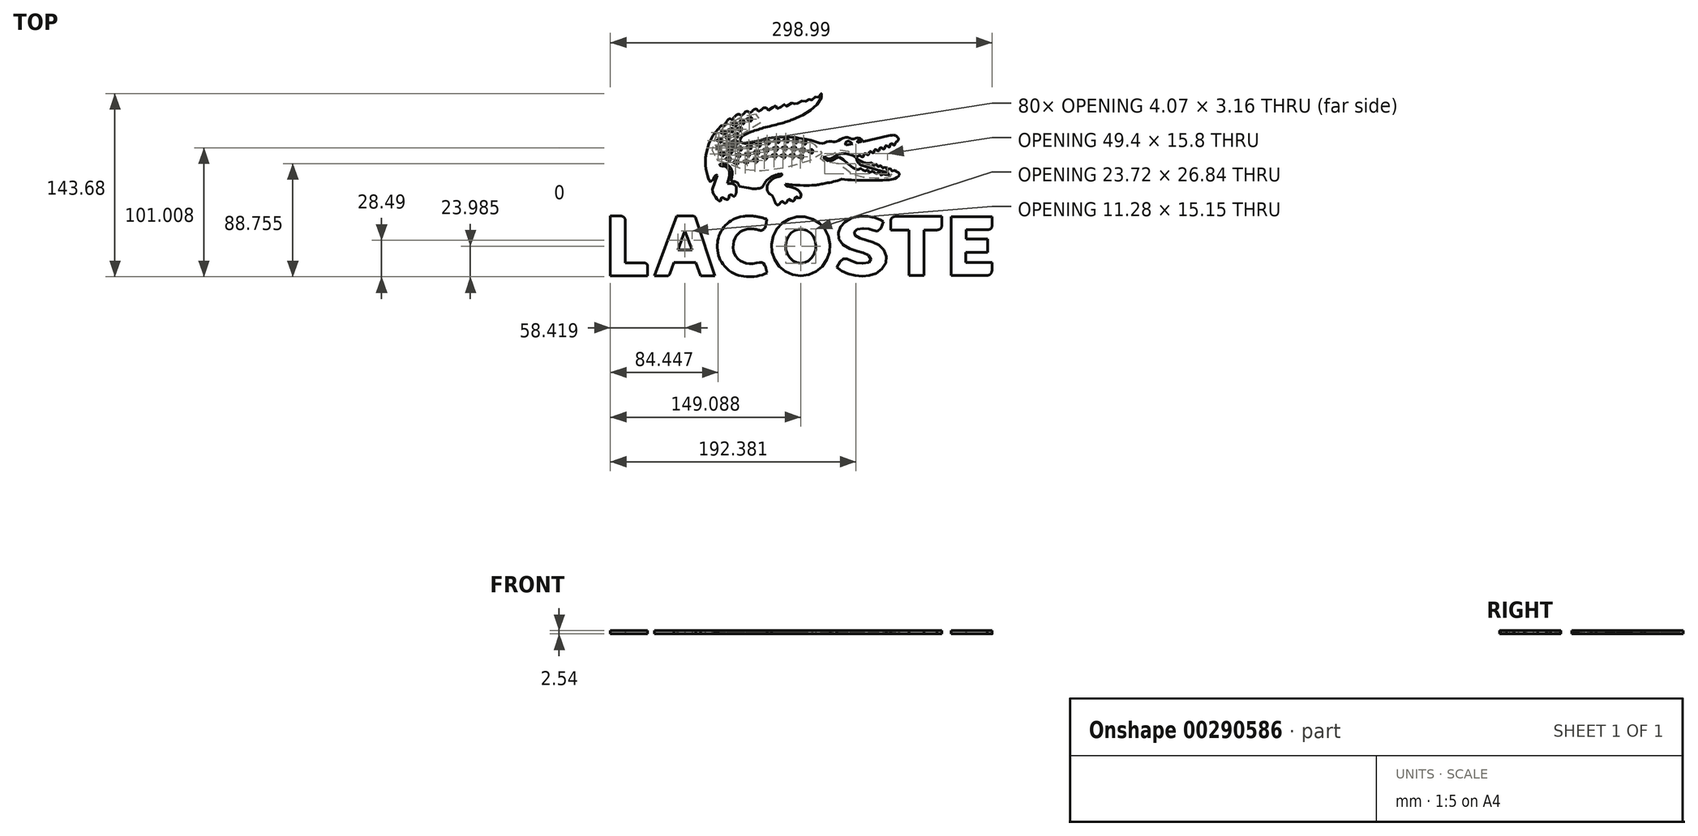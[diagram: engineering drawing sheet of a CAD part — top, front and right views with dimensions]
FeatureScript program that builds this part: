
annotation { "Feature Type Name" : "Feature", "Feature Type Description" : "" }
export const myFeature = defineFeature(function(context is Context, id is Id, definition is map)
    precondition{}
    {
        {
            var Q0;
            Q0=qCreatedBy(makeId("Top.planeOp"),FACE);
            var sketch = newSketch(context, id + "F0", { "sketchPlane" : qUnion([Q0])});
            skLineSegment(sketch, "E0", {"start": v(-126.74, -26.36) * mm, "end": v(-126.74, -73.35) * mm});
            skLineSegment(sketch, "E1", {"start": v(-126.74, -73.35) * mm, "end": v(-97.53, -73.35) * mm});
            skLineSegment(sketch, "E2", {"start": v(-97.53, -73.35) * mm, "end": v(-97.53, -65.73) * mm});
            skLineSegment(sketch, "E3", {"start": v(-100.07, -63.19) * mm, "end": v(-115.19, -63.19) * mm});
            skPoint(sketch, "E4.visualSharp", {"position": v(-97.53, -63.19) * mm});
            skArc(sketch, "E4.filletArc", {"start": v(-97.53, -65.73) * mm, "mid": v(-98.27, -63.93) * mm, "end": v(-100.07, -63.19) * mm});
            skPoint(sketch, "E5.visualSharp", {"position": v(-115.38, -25.09) * mm});
            skLineSegment(sketch, "E6", {"start": v(-126.74, -26.36) * mm, "end": v(-118.4, -26.36) * mm});
            skLineSegment(sketch, "E7", {"start": v(-115.22, -29.53) * mm, "end": v(-115.19, -63.19) * mm});
            skPoint(sketch, "E8.visualSharp", {"position": v(-115.22, -26.36) * mm});
            skArc(sketch, "E8.filletArc", {"start": v(-115.22, -29.53) * mm, "mid": v(-116.15, -27.29) * mm, "end": v(-118.4, -26.36) * mm});
            skLineSegment(sketch, "E9", {"start": v(-92.44, -73.35) * mm, "end": v(-74.98, -26.36) * mm});
            skLineSegment(sketch, "E10", {"start": v(-74.98, -26.36) * mm, "end": v(-62.15, -26.35) * mm});
            skLineSegment(sketch, "E11", {"start": v(-59.73, -28.1) * mm, "end": v(-45.04, -73.35) * mm});
            skLineSegment(sketch, "E12", {"start": v(-45.04, -73.35) * mm, "end": v(-56.2, -73.36) * mm});
            skLineSegment(sketch, "E13", {"start": v(-56.2, -73.36) * mm, "end": v(-59.86, -62.9) * mm});
            skLineSegment(sketch, "E14", {"start": v(-59.86, -62.9) * mm, "end": v(-77.03, -62.9) * mm});
            skLineSegment(sketch, "E15", {"start": v(-77.03, -62.9) * mm, "end": v(-80.3, -71.7) * mm});
            skLineSegment(sketch, "E16", {"start": v(-82.68, -73.35) * mm, "end": v(-92.44, -73.35) * mm});
            skPoint(sketch, "E17.visualSharp", {"position": v(-80.92, -73.35) * mm});
            skArc(sketch, "E17.filletArc", {"start": v(-82.68, -73.35) * mm, "mid": v(-81.23, -72.9) * mm, "end": v(-80.3, -71.7) * mm});
            skPoint(sketch, "E18.visualSharp", {"position": v(-60.3, -26.35) * mm});
            skArc(sketch, "E18.filletArc", {"start": v(-59.73, -28.1) * mm, "mid": v(-60.66, -26.83) * mm, "end": v(-62.15, -26.35) * mm});
            skLineSegment(sketch, "E19", {"start": v(-73.96, -53.02) * mm, "end": v(-68.33, -37.86) * mm});
            skLineSegment(sketch, "E20", {"start": v(-73.96, -53.02) * mm, "end": v(-62.68, -53.02) * mm});
            skLineSegment(sketch, "E21", {"start": v(-62.68, -53.02) * mm, "end": v(-68.33, -37.86) * mm});
            skArc(sketch, "E22", {"start": v(-22.8, -26.67) * mm, "mid": v(-36.65, -33.59) * mm, "end": v(-42.88, -47.77) * mm});
            skFitSpline(sketch, "E23", {"points": [v(-22.8, -26.67) * mm, v(-12.94, -26.67) * mm, v(-4.25, -28.89) * mm], "startDerivative": vector(21.68, 4.28) * mm, "endDerivative": vector(17.37, -6.77) * mm});
            skFitSpline(sketch, "E24", {"points": [v(-4.25, -28.89) * mm, v(-5.17, -33.86) * mm, v(-6.83, -36.92) * mm, v(-9.2, -37.59) * mm, v(-12.8, -36.7) * mm, v(-19.15, -36.46) * mm], "startDerivative": vector(-3.17, -23.27) * mm, "endDerivative": vector(-27.28, -0.67) * mm});
            skFitSpline(sketch, "E25", {"points": [v(-19.15, -36.46) * mm, v(-22.65, -37.5) * mm, v(-26.5, -39.93) * mm, v(-29.25, -43.78) * mm, v(-30.5, -49.4) * mm, v(-29.9, -55.03) * mm, v(-27.1, -59.6) * mm, v(-22.68, -62.67) * mm, v(-16.57, -63.79) * mm, v(-9.58, -62.6) * mm, v(-7.29, -62.94) * mm, v(-5.65, -65.1) * mm, v(-4.15, -70.91) * mm], "startDerivative": vector(-47.82, -11.43) * mm, "endDerivative": vector(13.68, -69.44) * mm});
            skArc(sketch, "E26", {"start": v(-42.88, -47.77) * mm, "mid": v(-42.97, -51.46) * mm, "end": v(-42.43, -55.11) * mm});
            skPoint(sketch, "E27.center.orphan", {"position": v(-20.17, -53.24) * mm});
            skFitSpline(sketch, "E28", {"points": [v(-42.43, -55.11) * mm, v(-39.32, -63.08) * mm, v(-31.41, -70.65) * mm, v(-22.68, -73.62) * mm, v(-13.21, -73.62) * mm, v(-4.15, -70.91) * mm], "startDerivative": vector(7.53, -52.18) * mm, "endDerivative": vector(40.9, 22.15) * mm});
            skArc(sketch, "E29.trimOffspring", {"start": v(-5.77, -64.84) * mm, "mid": v(-4.42, -63.24) * mm, "end": v(-3.23, -61.53) * mm});
            skEllipse(sketch, "E30", {"center": v(22.35, -49.95) * mm, "majorRadius": 23.23 * mm, "minorRadius": 23.02 * mm, "majorAxis": v(0, -1)});
            skEllipse(sketch, "E31", {"center": v(22.35, -49.95) * mm, "majorRadius": 13.42 * mm, "minorRadius": 11.86 * mm, "majorAxis": v(0, -1)});
            skFitSpline(sketch, "E32", {"points": [v(87.17, -30.8) * mm, v(83.6, -28.79) * mm, v(76.69, -27) * mm, v(64.74, -27.08) * mm, v(54.98, -32.69) * mm, v(51.81, -39.35) * mm, v(53.6, -46.83) * mm, v(63.52, -52.93) * mm, v(71.54, -55.3) * mm, v(76.45, -58.13) * mm, v(77.01, -61.55) * mm, v(72.14, -63.5) * mm, v(64.82, -62.6) * mm, v(59.94, -60.5) * mm, v(56.85, -59.52) * mm, v(54.25, -60.74) * mm, v(50.67, -66.59) * mm], "startDerivative": vector(-65.13, 47.63) * mm, "endDerivative": vector(-55.42, -106.59) * mm});
            skFitSpline(sketch, "E33", {"points": [v(50.67, -66.59) * mm, v(58.36, -71.4) * mm, v(69.3, -73.41) * mm, v(80.26, -71.73) * mm, v(88.4, -64.32) * mm, v(88.4, -54.72) * mm, v(81.08, -47.8) * mm, v(71.73, -44.72) * mm, v(64.9, -41.55) * mm, v(64.25, -39.11) * mm, v(67.26, -36.5) * mm, v(75.01, -36.34) * mm, v(78.67, -37.37) * mm, v(83.24, -38) * mm, v(87.17, -30.8) * mm], "startDerivative": vector(73.41, -63) * mm, "endDerivative": vector(50.37, 126.81) * mm});
            skLineSegment(sketch, "E34", {"start": v(107.14, -73.07) * mm, "end": v(107.14, -37.39) * mm});
            skLineSegment(sketch, "E35", {"start": v(107.14, -37.39) * mm, "end": v(92.8, -37.39) * mm});
            skLineSegment(sketch, "E36", {"start": v(92.8, -37.39) * mm, "end": v(92.8, -30.06) * mm});
            skLineSegment(sketch, "E37", {"start": v(107.14, -73.07) * mm, "end": v(118.77, -73.07) * mm});
            skLineSegment(sketch, "E38", {"start": v(118.77, -73.07) * mm, "end": v(118.77, -37.28) * mm});
            skLineSegment(sketch, "E39", {"start": v(118.77, -37.28) * mm, "end": v(129.11, -37.28) * mm});
            skFitSpline(sketch, "E40", {"points": [v(92.8, -30.06) * mm, v(93.55, -27.9) * mm, v(96.03, -26.72) * mm], "startDerivative": vector(0.83, 5.06) * mm, "endDerivative": vector(5.56, 1.68) * mm});
            skLineSegment(sketch, "E41", {"start": v(96.03, -26.72) * mm, "end": v(132.77, -26.72) * mm});
            skLineSegment(sketch, "E42", {"start": v(132.77, -26.72) * mm, "end": v(132.77, -34.2) * mm});
            skFitSpline(sketch, "E43", {"points": [v(129.11, -37.28) * mm, v(131.7, -36.34) * mm, v(132.77, -34.2) * mm], "startDerivative": vector(6.35, 1.16) * mm, "endDerivative": vector(1.9, 7.6) * mm});
            skLineSegment(sketch, "E44", {"start": v(172.25, -33.98) * mm, "end": v(172.25, -26.74) * mm});
            skLineSegment(sketch, "E45", {"start": v(172.25, -26.74) * mm, "end": v(140.16, -26.74) * mm});
            skLineSegment(sketch, "E46", {"start": v(140.16, -26.74) * mm, "end": v(140.16, -73) * mm});
            skLineSegment(sketch, "E47", {"start": v(140.16, -73) * mm, "end": v(168.36, -73) * mm});
            skLineSegment(sketch, "E48", {"start": v(172.17, -68.8) * mm, "end": v(172.17, -62.63) * mm});
            skLineSegment(sketch, "E49", {"start": v(172.17, -62.63) * mm, "end": v(151.6, -62.63) * mm});
            skLineSegment(sketch, "E50", {"start": v(151.6, -62.63) * mm, "end": v(151.6, -54.79) * mm});
            skLineSegment(sketch, "E51", {"start": v(151.6, -54.79) * mm, "end": v(168.59, -54.79) * mm});
            skLineSegment(sketch, "E52", {"start": v(168.59, -54.79) * mm, "end": v(168.59, -44.27) * mm});
            skLineSegment(sketch, "E53", {"start": v(168.59, -44.27) * mm, "end": v(151.75, -44.27) * mm});
            skLineSegment(sketch, "E54", {"start": v(151.75, -44.27) * mm, "end": v(151.75, -37.18) * mm});
            skLineSegment(sketch, "E55", {"start": v(151.75, -37.18) * mm, "end": v(168.36, -37.18) * mm});
            skFitSpline(sketch, "E56", {"points": [v(168.36, -37.18) * mm, v(171.1, -36.34) * mm, v(172.25, -33.98) * mm], "startDerivative": vector(6.59, 0.9) * mm, "endDerivative": vector(1.87, 7.95) * mm});
            skFitSpline(sketch, "E57", {"points": [v(172.17, -68.8) * mm, v(170.95, -71.78) * mm, v(168.36, -73) * mm], "startDerivative": vector(-1.37, -10.07) * mm, "endDerivative": vector(-10.1, -1.84) * mm});
            skSolve(sketch);
        }
        {
            var Q0;
            Q0=makeQuery(id+"F0.imprint","IMPRINT",FACE,{"disambiguationData":[TD([[makeQuery(id+"F0.imprint","IMPRINT",EDGE,{"derivedFrom":sQuery(id+"F0.wireOp",EDGE,"E0")}),1.0]])]});
            var Q1;
            Q1=makeQuery(id+"F0.imprint","IMPRINT",FACE,{"disambiguationData":[TD([[makeQuery(id+"F0.imprint","IMPRINT",EDGE,{"derivedFrom":sQuery(id+"F0.wireOp",EDGE,"E9")}),-1.0]])]});
            var Q2;
            Q2=makeQuery(id+"F0.imprint","IMPRINT",FACE,{"disambiguationData":[TD([[makeQuery(id+"F0.imprint","IMPRINT",EDGE,{"derivedFrom":sQuery(id+"F0.wireOp",EDGE,"E22")}),1.0]])]});
            var Q3;
            Q3=makeQuery(id+"F0.imprint","IMPRINT",FACE,{"disambiguationData":[TD([[makeQuery(id+"F0.imprint","IMPRINT",EDGE,{"derivedFrom":sQuery(id+"F0.wireOp",EDGE,"E30")}),1.0]])]});
            var Q4;
            Q4=makeQuery(id+"F0.imprint","IMPRINT",FACE,{"disambiguationData":[TD([[makeQuery(id+"F0.imprint","IMPRINT",EDGE,{"derivedFrom":sQuery(id+"F0.wireOp",EDGE,"E32")}),1.0]])]});
            var Q5;
            Q5=makeQuery(id+"F0.imprint","IMPRINT",FACE,{"disambiguationData":[TD([[makeQuery(id+"F0.imprint","IMPRINT",EDGE,{"derivedFrom":sQuery(id+"F0.wireOp",EDGE,"E34")}),-1.0]])]});
            var Q6;
            Q6=makeQuery(id+"F0.imprint","IMPRINT",FACE,{"disambiguationData":[TD([[makeQuery(id+"F0.imprint","IMPRINT",EDGE,{"derivedFrom":sQuery(id+"F0.wireOp",EDGE,"E44")}),1.0]])]});
            extrude(context, id + "F1", {"entities" : qUnion([Q0, Q1, Q2, Q3, Q4, Q5, Q6]), "depth" : 2.54 * mm});
        }
        {
            var Q0;
            Q0=qCreatedBy(makeId("Top.planeOp"),FACE);
            var sketch = newSketch(context, id + "F2", { "sketchPlane" : qUnion([Q0])});
            skFitSpline(sketch, "E58", {"points": [v(-33.16, -9.8) * mm, v(-31.82, -9.75) * mm, v(-30.48, -10.73) * mm, v(-29.55, -10.73) * mm, v(-28.16, -8.13) * mm], "startDerivative": vector(6.07, 1.44) * mm, "endDerivative": vector(3.91, 9.96) * mm});
            skFitSpline(sketch, "E59", {"points": [v(-28.16, -8.13) * mm, v(-28.16, -3.92) * mm], "startDerivative": vector(0, 4.22) * mm, "endDerivative": vector(0, 4.22) * mm});
            skFitSpline(sketch, "E60", {"points": [v(-28.16, -3.92) * mm, v(-28.6, -2.62) * mm, v(-30.38, -1.28) * mm], "startDerivative": vector(-0.87, 3.34) * mm, "endDerivative": vector(-3.8, 2.24) * mm});
            skFitSpline(sketch, "E61", {"points": [v(-30.38, -1.28) * mm, v(-35.23, -0.71) * mm], "startDerivative": vector(-3.93, 1.7) * mm, "endDerivative": vector(-4.72, 0.42) * mm});
            skFitSpline(sketch, "E62", {"points": [v(-35.23, -0.71) * mm, v(-33.63, 5.12) * mm, v(-33.7, 8.88) * mm, v(-35.23, 11.4) * mm, v(-37.41, 12.77) * mm, v(-40.35, 13) * mm, v(-40.9, 13.42) * mm, v(-41.08, 14.3) * mm], "startDerivative": vector(4.9, 23.15) * mm, "endDerivative": vector(2.82, 11.86) * mm});
            skFitSpline(sketch, "E63", {"points": [v(-33.16, -9.8) * mm, v(-33.68, -10.3) * mm, v(-34.2, -12.63) * mm, v(-35.09, -13.47) * mm, v(-36.8, -13.01) * mm, v(-38.13, -12.14) * mm, v(-39.5, -11.95) * mm, v(-40.15, -12.7) * mm, v(-40.27, -13.97) * mm, v(-40.73, -14.58) * mm, v(-41.87, -14.39) * mm, v(-46.63, -7.9) * mm], "startDerivative": vector(-9.57, -5.5) * mm, "endDerivative": vector(-26.48, 42.47) * mm});
            skFitSpline(sketch, "E64", {"points": [v(-46.63, -7.9) * mm, v(-46.84, -5.25) * mm], "startDerivative": vector(-0.21, 2.66) * mm, "endDerivative": vector(-0.21, 2.66) * mm});
            skFitSpline(sketch, "E65", {"points": [v(-46.84, -5.25) * mm, v(-43.16, 5.41) * mm], "startDerivative": vector(3.68, 10.66) * mm, "endDerivative": vector(3.68, 10.66) * mm});
            skFitSpline(sketch, "E66", {"points": [v(-43.16, 5.41) * mm, v(-43.16, 5.76) * mm, v(-44.08, 5.76) * mm, v(-45.18, 4.72) * mm, v(-46.63, 1.75) * mm, v(-47.86, 0.87) * mm, v(-48.8, 0.8) * mm, v(-50.1, 3.4) * mm, v(-51.72, 10.2) * mm, v(-52.08, 20.08) * mm, v(-47.82, 34.36) * mm, v(-40.35, 44.17) * mm], "startDerivative": vector(4.33, 14.89) * mm, "endDerivative": vector(50.94, 58.96) * mm});
            skFitSpline(sketch, "E67", {"points": [v(-40.35, 44.17) * mm, v(-39.97, 44.74) * mm, v(-38.78, 44.17) * mm, v(-34.54, 49.27) * mm, v(-33.1, 49.85) * mm, v(-32.1, 49.25) * mm], "startDerivative": vector(6.96, 5.98) * mm, "endDerivative": vector(5.99, -6.7) * mm});
            skFitSpline(sketch, "E68", {"points": [v(-32.1, 49.25) * mm, v(-31.52, 49.25) * mm, v(-30.26, 50.46) * mm, v(-27.02, 53.55) * mm, v(-25.48, 53.16) * mm, v(-24.3, 52.62) * mm, v(-21.92, 54.34) * mm, v(-20.48, 55.61) * mm, v(-19, 55.9) * mm, v(-18.44, 55.09) * mm, v(-17.22, 54.77) * mm, v(-15.03, 56.62) * mm, v(-13.23, 57.63) * mm], "startDerivative": vector(12.35, -2.62) * mm, "endDerivative": vector(20.2, 8.3) * mm});
            skFitSpline(sketch, "E69", {"points": [v(-13.23, 57.63) * mm, v(-12.27, 57.63) * mm, v(-11.4, 56.4) * mm, v(-10.95, 56.05) * mm, v(-10.18, 56) * mm, v(-6.53, 58.68) * mm], "startDerivative": vector(6.18, 1.68) * mm, "endDerivative": vector(11.93, 10.26) * mm});
            skFitSpline(sketch, "E70", {"points": [v(-6.53, 58.68) * mm, v(-5.67, 59.01) * mm, v(-4.8, 58.68) * mm, v(-4.54, 57.83) * mm, v(-3.8, 57) * mm, v(-2.23, 56.86) * mm, v(0.65, 59.3) * mm, v(1.88, 60.13) * mm, v(2.7, 59.99) * mm, v(3.13, 59.06) * mm, v(3.85, 58.04) * mm, v(4.97, 57.83) * mm, v(7.1, 59.53) * mm, v(9.08, 61.1) * mm, v(9.9, 60.91) * mm, v(10.6, 60) * mm, v(11.38, 59.78) * mm, v(15.66, 62.34) * mm, v(16.39, 62.34) * mm, v(17.22, 61.8) * mm, v(18.35, 61.35) * mm, v(19.3, 61.48) * mm, v(22.07, 64.04) * mm, v(24.36, 63.18) * mm, v(25.6, 63.12) * mm, v(27.81, 65.06) * mm, v(29.13, 65.12) * mm, v(29.7, 64.58) * mm, v(30.75, 64.47) * mm, v(32.8, 66.65) * mm, v(34.03, 66.94) * mm, v(35.12, 66.6) * mm, v(36.24, 66.94) * mm, v(38.17, 69.63) * mm, v(38.72, 69.6) * mm, v(38.6, 66.7) * mm, v(34.57, 60.62) * mm, v(27.65, 55.04) * mm, v(15.85, 49.25) * mm], "startDerivative": vector(44.69, 26.17) * mm, "endDerivative": vector(-212.73, -79.77) * mm});
            skFitSpline(sketch, "E71", {"points": [v(-41.08, 14.3) * mm, v(-37.29, 14.3) * mm, v(-33.9, 13) * mm, v(-31.7, 9.7) * mm, v(-31.37, 6.35) * mm, v(-32.21, 0.9) * mm], "startDerivative": vector(19.64, 1.15) * mm, "endDerivative": vector(-3.96, -20.19) * mm});
            skFitSpline(sketch, "E72", {"points": [v(-32.21, 0.9) * mm, v(-29.12, 0.61) * mm, v(-27.6, 0) * mm, v(-26.56, -1.29) * mm, v(-25.95, -2.96) * mm], "startDerivative": vector(9.82, -0.81) * mm, "endDerivative": vector(2.23, -7.43) * mm});
            skFitSpline(sketch, "E73", {"points": [v(-25.95, -2.96) * mm, v(-17, -4.67) * mm, v(-12.13, -4.85) * mm, v(-8.22, -3.84) * mm, v(-6.01, -0.8) * mm, v(-2.33, 3.23) * mm, v(4.19, 6.29) * mm, v(7.33, 6.67) * mm, v(7.6, 6.08) * mm, v(6.06, 4.9) * mm, v(3.84, 4.35) * mm, v(0, 2.54) * mm, v(-4.04, -3.23) * mm, v(-2.75, -8.37) * mm, v(0, -10.45) * mm, v(2.8, -16.61) * mm, v(4.26, -17.66) * mm], "startDerivative": vector(101.91, -23.85) * mm, "endDerivative": vector(37.13, -13.37) * mm});
            skFitSpline(sketch, "E74", {"points": [v(4.19, 6.29) * mm, v(7.33, 6.67) * mm], "startDerivative": vector(3.2, 0.35) * mm, "endDerivative": vector(3.2, 0.35) * mm});
            skFitSpline(sketch, "E75.trimOffspring", {"points": [v(-25.95, -2.96) * mm, v(-17, -4.67) * mm, v(-12.13, -4.85) * mm, v(-8.22, -3.84) * mm, v(-6.01, -0.8) * mm, v(-2.33, 3.23) * mm, v(4.19, 6.29) * mm, v(7.33, 6.67) * mm, v(7.6, 6.08) * mm, v(6.06, 4.9) * mm, v(3.84, 4.35) * mm, v(0, 2.54) * mm, v(-4.04, -3.23) * mm, v(-2.75, -8.37) * mm, v(0, -10.45) * mm, v(2.8, -16.61) * mm, v(4.26, -17.66) * mm], "startDerivative": vector(101.91, -23.85) * mm, "endDerivative": vector(37.13, -13.37) * mm});
            skFitSpline(sketch, "E76", {"points": [v(4.26, -17.66) * mm, v(5.5, -16.98) * mm, v(7.06, -14.92) * mm, v(8.22, -14.81) * mm, v(9.28, -16.02) * mm, v(10.6, -16.48) * mm, v(11.56, -15.22) * mm, v(12.75, -13.09) * mm, v(14.54, -13.98) * mm, v(16.3, -14.72) * mm, v(17.54, -13.55) * mm, v(17.97, -11.6) * mm, v(19.33, -11.41) * mm, v(21.08, -12.5) * mm, v(22.56, -10.17) * mm, v(21.04, -6.9) * mm, v(17.53, -4.58) * mm, v(11.93, -2.88) * mm, v(10.48, -2.01) * mm, v(10.39, -1.18) * mm, v(18.27, -2.17) * mm], "startDerivative": vector(33.67, 9.78) * mm, "endDerivative": vector(117.27, -26.16) * mm});
            skFitSpline(sketch, "E77", {"points": [v(0, -10.45) * mm, v(1.73, -13.42) * mm, v(2.8, -16.61) * mm], "startDerivative": vector(4.48, -4.79) * mm, "endDerivative": vector(1.83, -6.54) * mm});
            skFitSpline(sketch, "E78", {"points": [v(10.39, -1.18) * mm, v(18.27, -2.17) * mm], "startDerivative": vector(7.88, -0.99) * mm, "endDerivative": vector(7.88, -0.99) * mm});
            skFitSpline(sketch, "E79", {"points": [v(18.27, -2.17) * mm, v(35.82, -1.76) * mm, v(41.87, -0.6) * mm, v(54.33, 2.76) * mm], "startDerivative": vector(85.5, -2.33) * mm, "endDerivative": vector(35.55, 16.97) * mm});
            skFitSpline(sketch, "E80", {"points": [v(54.33, 2.76) * mm, v(68.2, 1.68) * mm, v(90.43, 1.96) * mm, v(95.4, 2.76) * mm, v(99.16, 5.24) * mm, v(99.23, 7.4) * mm, v(97.4, 8.49) * mm, v(96.45, 9.57) * mm], "startDerivative": vector(56.47, -8.99) * mm, "endDerivative": vector(-19.43, 40.25) * mm});
            skFitSpline(sketch, "E81", {"points": [v(96.45, 9.57) * mm, v(95.82, 9.57) * mm, v(94.55, 8.95) * mm, v(93.6, 9.01) * mm, v(93, 10.16) * mm, v(92.58, 10.75) * mm, v(92.02, 10.81) * mm, v(90.94, 10.35) * mm, v(90.25, 10.06) * mm, v(89.44, 11.01) * mm, v(88.88, 11.93) * mm, v(87.04, 11.34) * mm, v(86.39, 11.24) * mm, v(85.4, 13.02) * mm, v(84.69, 13.15) * mm, v(83.34, 12.5) * mm, v(82.79, 12.52) * mm, v(82.4, 12.98) * mm, v(81.94, 14.1) * mm, v(81.21, 14.36) * mm, v(79.6, 13.6) * mm, v(78.86, 13.77) * mm, v(78.2, 15.25) * mm, v(77.25, 15.58) * mm, v(76.53, 15.18) * mm, v(74.63, 14.89) * mm, v(70.08, 16.37) * mm, v(67.1, 18.27) * mm], "startDerivative": vector(-21.72, 4.04) * mm, "endDerivative": vector(-38.6, 34.59) * mm});
            skFitSpline(sketch, "E82", {"points": [v(67.1, 18.27) * mm, v(66.54, 18.27) * mm], "startDerivative": vector(-0.56, 0) * mm, "endDerivative": vector(-0.56, 0) * mm});
            skFitSpline(sketch, "E83", {"points": [v(66.54, 18.27) * mm, v(65.5, 20.44) * mm], "startDerivative": vector(-1.05, 2) * mm, "endDerivative": vector(-1.05, 2) * mm});
            skFitSpline(sketch, "E84", {"points": [v(65.5, 20.44) * mm, v(66.86, 20.44) * mm], "startDerivative": vector(1.37, 0) * mm, "endDerivative": vector(1.37, 0) * mm});
            skFitSpline(sketch, "E85", {"points": [v(66.86, 20.44) * mm, v(68.11, 21.15) * mm, v(68.3, 21.29) * mm], "startDerivative": vector(2.15, 1.17) * mm, "endDerivative": vector(0.49, 0.41) * mm});
            skFitSpline(sketch, "E86", {"points": [v(68.11, 21.15) * mm, v(68.54, 21.24) * mm, v(69.12, 21.15) * mm, v(70.07, 20.18) * mm, v(70.9, 20.02) * mm, v(71.48, 20.42) * mm, v(71.73, 22.04) * mm, v(72.4, 22.77) * mm, v(73.65, 22.38) * mm, v(74.58, 21.57) * mm, v(75.48, 21.82) * mm, v(75.72, 23.11) * mm, v(76.35, 24.2) * mm, v(77.2, 24.23) * mm, v(78.5, 23.24) * mm, v(79.44, 23.27) * mm, v(79.92, 24.4) * mm], "startDerivative": vector(10.17, 2.59) * mm, "endDerivative": vector(2.45, 24.6) * mm});
            skFitSpline(sketch, "E87", {"points": [v(79.92, 24.4) * mm, v(80.33, 25.65) * mm, v(81.18, 25.84) * mm, v(82.53, 24.73) * mm, v(83.63, 24.79) * mm, v(84.07, 26.4) * mm, v(84.68, 27.28) * mm, v(85.75, 27.14) * mm, v(86.75, 26.23) * mm, v(87.8, 26.3) * mm, v(88.29, 27.91) * mm, v(88.87, 28.88) * mm, v(89.86, 28.69) * mm, v(90.88, 27.86) * mm, v(91.79, 27.75) * mm, v(92.25, 28.97) * mm, v(92.67, 30.18) * mm, v(93.74, 30.4) * mm, v(94.87, 29.46) * mm], "startDerivative": vector(4.1, 25.42) * mm, "endDerivative": vector(16.22, -13.1) * mm});
            skFitSpline(sketch, "E88", {"points": [v(94.87, 29.46) * mm, v(95.62, 29.21) * mm, v(96.3, 29.77) * mm, v(96.47, 31.04) * mm, v(97.21, 31.79) * mm, v(98.53, 32.67) * mm, v(98.73, 34.3) * mm, v(97.96, 35.71) * mm, v(96.2, 36.96) * mm, v(91.07, 36.54) * mm], "startDerivative": vector(9.48, -5.38) * mm, "endDerivative": vector(-31.21, -6.75) * mm});
            skLineSegment(sketch, "E89", {"start": v(71.76, 32.17) * mm, "end": v(91.07, 36.54) * mm});
            skLineSegment(sketch, "E90", {"start": v(71.76, 32.17) * mm, "end": v(71.07, 32.17) * mm});
            skFitSpline(sketch, "E91", {"points": [v(71.07, 32.17) * mm, v(69.92, 33.75) * mm, v(68.27, 34.86) * mm], "startDerivative": vector(-2.08, 3.4) * mm, "endDerivative": vector(-3.53, 1.96) * mm});
            skFitSpline(sketch, "E92", {"points": [v(68.27, 34.86) * mm, v(66.36, 34.86) * mm, v(64.4, 34.28) * mm, v(61.74, 34.33) * mm, v(59.59, 35.1) * mm, v(56.5, 35.1) * mm, v(52.57, 33.25) * mm, v(50.22, 31.95) * mm, v(48.52, 31.73) * mm, v(46.86, 32.17) * mm, v(43.7, 32.17) * mm, v(40.3, 30.87) * mm, v(37, 30.96) * mm, v(20.7, 34.86) * mm], "startDerivative": vector(-33.2, 2.97) * mm, "endDerivative": vector(-113.65, 8.5) * mm});
            skFitSpline(sketch, "E93", {"points": [v(20.7, 34.86) * mm, v(12.28, 35.63) * mm, v(0.85, 35.2) * mm, v(-5.24, 34.2) * mm, v(-15.18, 31.36) * mm, v(-21.43, 30.74) * mm, v(-24.12, 31.46) * mm, v(-25.23, 32.9) * mm, v(-23.86, 35.85) * mm, v(-16.39, 39.75) * mm], "startDerivative": vector(-59.78, 7.95) * mm, "endDerivative": vector(67.19, 26.75) * mm});
            skFitSpline(sketch, "E94", {"points": [v(-16.39, 39.75) * mm, v(-5.55, 43.15) * mm, v(8.28, 46.66) * mm, v(15.85, 49.25) * mm], "startDerivative": vector(30.24, 10.28) * mm, "endDerivative": vector(24.17, 9.17) * mm});
            skSolve(sketch);
        }
        {
            var Q0;
            Q0 = qSketchRegion(id + "F2", true);
            extrude(context, id + "F3", {"entities" : qUnion([Q0]), "depth" : 2.54 * mm});
        }
        {
            var Q0;
            Q0=qCreatedBy(makeId("Top.planeOp"),FACE);
            var sketch = newSketch(context, id + "F4", { "sketchPlane" : qUnion([Q0])});
            skFitSpline(sketch, "E95", {"points": [v(-12.63, 53.57) * mm, v(-31.6, 47.42) * mm, v(-44.42, 36.65) * mm, v(-45.96, 19.48) * mm, v(-35.96, 15.64) * mm, v(-20.58, 9.74) * mm, v(24.28, 15.38) * mm, v(39.14, 24.35) * mm, v(30.94, 31.02) * mm, v(27.4, 32.96) * mm, v(16.2, 34.93) * mm, v(0, 34.38) * mm, v(-11.23, 31.6) * mm, v(-20.26, 29.77) * mm, v(-25.36, 31.26) * mm, v(-26.44, 34.52) * mm, v(-18.3, 41.85) * mm, v(-8.52, 47.7) * mm, v(-12.63, 53.57) * mm]});
            skSolve(sketch);
        }
        {
            var Q0;
            Q0 = qSketchRegion(id + "F4", true);
            extrude(context, id + "F5", {"entities" : qUnion([Q0]), "depth" : 2.54 * mm});
        }
        {
            var Q0;
            Q0=makeQuery(id+"F3.opExtrude","CAP_FACE",FACE,{"disambiguationData":[OSD([sQuery(id+"F2.wireOp",EDGE,"E58"),sQuery(id+"F2.wireOp",EDGE,"E59"),sQuery(id+"F2.wireOp",EDGE,"E60"),sQuery(id+"F2.wireOp",EDGE,"E61"),sQuery(id+"F2.wireOp",EDGE,"E62"),sQuery(id+"F2.wireOp",EDGE,"E63"),sQuery(id+"F2.wireOp",EDGE,"E64"),sQuery(id+"F2.wireOp",EDGE,"E65"),sQuery(id+"F2.wireOp",EDGE,"E66"),sQuery(id+"F2.wireOp",EDGE,"E67"),sQuery(id+"F2.wireOp",EDGE,"E68"),sQuery(id+"F2.wireOp",EDGE,"E69"),sQuery(id+"F2.wireOp",EDGE,"E70"),sQuery(id+"F2.wireOp",EDGE,"E71"),sQuery(id+"F2.wireOp",EDGE,"E72"),sQuery(id+"F2.wireOp",EDGE,"E73"),sQuery(id+"F2.wireOp",EDGE,"E74"),sQuery(id+"F2.wireOp",EDGE,"E75.trimOffspring"),sQuery(id+"F2.wireOp",EDGE,"E76"),sQuery(id+"F2.wireOp",EDGE,"E77"),sQuery(id+"F2.wireOp",EDGE,"E75.trimOffspring"),sQuery(id+"F2.wireOp",EDGE,"E78"),sQuery(id+"F2.wireOp",EDGE,"E79"),sQuery(id+"F2.wireOp",EDGE,"E80"),sQuery(id+"F2.wireOp",EDGE,"E81"),sQuery(id+"F2.wireOp",EDGE,"E82"),sQuery(id+"F2.wireOp",EDGE,"E83"),sQuery(id+"F2.wireOp",EDGE,"E84"),sQuery(id+"F2.wireOp",EDGE,"E85"),sQuery(id+"F2.wireOp",EDGE,"E86"),sQuery(id+"F2.wireOp",EDGE,"E87"),sQuery(id+"F2.wireOp",EDGE,"E88"),sQuery(id+"F2.wireOp",EDGE,"E89"),sQuery(id+"F2.wireOp",EDGE,"E90"),sQuery(id+"F2.wireOp",EDGE,"E91"),sQuery(id+"F2.wireOp",EDGE,"E92"),sQuery(id+"F2.wireOp",EDGE,"E93"),sQuery(id+"F2.wireOp",EDGE,"E94")])],"isStart":false});
            var sketch = newSketch(context, id + "F6", { "sketchPlane" : qUnion([Q0])});
            skFitSpline(sketch, "E96", {"points": [v(-16.48, 51.11) * mm, v(-16.7, 47.95) * mm], "startDerivative": vector(2.21, -2.53) * mm, "endDerivative": vector(-2.53, -2.53) * mm});
            skFitSpline(sketch, "E97", {"points": [v(-16.48, 51.11) * mm, v(-20.07, 49.74) * mm], "startDerivative": vector(-3.48, -0.63) * mm, "endDerivative": vector(-3.59, -1.37) * mm});
            skFitSpline(sketch, "E98", {"points": [v(-20.07, 49.74) * mm, v(-16.7, 47.95) * mm], "startDerivative": vector(3.37, -1.8) * mm, "endDerivative": vector(3.48, -2.85) * mm});
            skFitSpline(sketch, "E99", {"points": [v(-22.43, 48.97) * mm, v(-22.64, 45.81) * mm], "startDerivative": vector(2.21, -2.53) * mm, "endDerivative": vector(-2.53, -2.53) * mm});
            skFitSpline(sketch, "E100", {"points": [v(-22.43, 48.97) * mm, v(-26.02, 47.6) * mm], "startDerivative": vector(-3.48, -0.63) * mm, "endDerivative": vector(-3.59, -1.37) * mm});
            skFitSpline(sketch, "E101", {"points": [v(-26.02, 47.6) * mm, v(-22.64, 45.81) * mm], "startDerivative": vector(3.37, -1.8) * mm, "endDerivative": vector(3.48, -2.85) * mm});
            skFitSpline(sketch, "E102", {"points": [v(-24.44, 43.33) * mm, v(-24.65, 40.17) * mm], "startDerivative": vector(2.21, -2.53) * mm, "endDerivative": vector(-2.53, -2.53) * mm});
            skFitSpline(sketch, "E103", {"points": [v(-24.44, 43.33) * mm, v(-28.03, 41.96) * mm], "startDerivative": vector(-3.48, -0.63) * mm, "endDerivative": vector(-3.59, -1.37) * mm});
            skFitSpline(sketch, "E104", {"points": [v(-28.03, 41.96) * mm, v(-24.65, 40.17) * mm], "startDerivative": vector(3.37, -1.8) * mm, "endDerivative": vector(3.48, -2.85) * mm});
            skFitSpline(sketch, "E105", {"points": [v(-28.3, 47.05) * mm, v(-28.5, 43.89) * mm], "startDerivative": vector(2.21, -2.53) * mm, "endDerivative": vector(-2.53, -2.53) * mm});
            skFitSpline(sketch, "E106", {"points": [v(-28.3, 47.05) * mm, v(-31.88, 45.68) * mm], "startDerivative": vector(-3.48, -0.63) * mm, "endDerivative": vector(-3.59, -1.37) * mm});
            skFitSpline(sketch, "E107", {"points": [v(-31.88, 45.68) * mm, v(-28.5, 43.89) * mm], "startDerivative": vector(3.37, -1.8) * mm, "endDerivative": vector(3.48, -2.85) * mm});
            skFitSpline(sketch, "E108", {"points": [v(-27.04, 38.52) * mm, v(-27.25, 35.36) * mm], "startDerivative": vector(2.21, -2.53) * mm, "endDerivative": vector(-2.53, -2.53) * mm});
            skFitSpline(sketch, "E109", {"points": [v(-27.04, 38.52) * mm, v(-30.63, 37.15) * mm], "startDerivative": vector(-3.48, -0.63) * mm, "endDerivative": vector(-3.59, -1.37) * mm});
            skFitSpline(sketch, "E110", {"points": [v(-30.63, 37.15) * mm, v(-27.25, 35.36) * mm], "startDerivative": vector(3.37, -1.8) * mm, "endDerivative": vector(3.48, -2.85) * mm});
            skFitSpline(sketch, "E111", {"points": [v(-31.24, 42.55) * mm, v(-31.46, 39.38) * mm], "startDerivative": vector(2.21, -2.53) * mm, "endDerivative": vector(-2.53, -2.53) * mm});
            skFitSpline(sketch, "E112", {"points": [v(-31.24, 42.55) * mm, v(-34.83, 41.18) * mm], "startDerivative": vector(-3.48, -0.63) * mm, "endDerivative": vector(-3.59, -1.37) * mm});
            skFitSpline(sketch, "E113", {"points": [v(-34.83, 41.18) * mm, v(-31.46, 39.38) * mm], "startDerivative": vector(3.37, -1.8) * mm, "endDerivative": vector(3.48, -2.85) * mm});
            skFitSpline(sketch, "E114", {"points": [v(-37.16, 40.6) * mm, v(-37.37, 37.43) * mm], "startDerivative": vector(2.21, -2.53) * mm, "endDerivative": vector(-2.53, -2.53) * mm});
            skFitSpline(sketch, "E115", {"points": [v(-37.16, 40.6) * mm, v(-40.75, 39.22) * mm], "startDerivative": vector(-3.48, -0.63) * mm, "endDerivative": vector(-3.59, -1.37) * mm});
            skFitSpline(sketch, "E116", {"points": [v(-40.75, 39.22) * mm, v(-37.37, 37.43) * mm], "startDerivative": vector(3.37, -1.8) * mm, "endDerivative": vector(3.48, -2.85) * mm});
            skFitSpline(sketch, "E117", {"points": [v(-33.61, 36.8) * mm, v(-33.82, 33.64) * mm], "startDerivative": vector(2.21, -2.53) * mm, "endDerivative": vector(-2.53, -2.53) * mm});
            skFitSpline(sketch, "E118", {"points": [v(-33.61, 36.8) * mm, v(-37.2, 35.43) * mm], "startDerivative": vector(-3.48, -0.63) * mm, "endDerivative": vector(-3.59, -1.37) * mm});
            skFitSpline(sketch, "E119", {"points": [v(-37.2, 35.43) * mm, v(-33.82, 33.64) * mm], "startDerivative": vector(3.37, -1.8) * mm, "endDerivative": vector(3.48, -2.85) * mm});
            skFitSpline(sketch, "E120", {"points": [v(-27.63, 32.78) * mm, v(-27.85, 29.62) * mm], "startDerivative": vector(2.21, -2.53) * mm, "endDerivative": vector(-2.53, -2.53) * mm});
            skFitSpline(sketch, "E121", {"points": [v(-27.63, 32.78) * mm, v(-31.22, 31.4) * mm], "startDerivative": vector(-3.48, -0.63) * mm, "endDerivative": vector(-3.59, -1.37) * mm});
            skFitSpline(sketch, "E122", {"points": [v(-31.22, 31.4) * mm, v(-27.85, 29.62) * mm], "startDerivative": vector(3.37, -1.8) * mm, "endDerivative": vector(3.48, -2.85) * mm});
            skFitSpline(sketch, "E123", {"points": [v(-24.39, 28.08) * mm, v(-24.6, 24.92) * mm], "startDerivative": vector(2.21, -2.53) * mm, "endDerivative": vector(-2.53, -2.53) * mm});
            skFitSpline(sketch, "E124", {"points": [v(-24.39, 28.08) * mm, v(-27.97, 26.71) * mm], "startDerivative": vector(-3.48, -0.63) * mm, "endDerivative": vector(-3.59, -1.37) * mm});
            skFitSpline(sketch, "E125", {"points": [v(-27.97, 26.71) * mm, v(-24.6, 24.92) * mm], "startDerivative": vector(3.37, -1.8) * mm, "endDerivative": vector(3.48, -2.85) * mm});
            skFitSpline(sketch, "E126", {"points": [v(-31.66, 26.04) * mm, v(-31.87, 22.88) * mm], "startDerivative": vector(2.21, -2.53) * mm, "endDerivative": vector(-2.53, -2.53) * mm});
            skFitSpline(sketch, "E127", {"points": [v(-31.66, 26.04) * mm, v(-35.25, 24.67) * mm], "startDerivative": vector(-3.48, -0.63) * mm, "endDerivative": vector(-3.59, -1.37) * mm});
            skFitSpline(sketch, "E128", {"points": [v(-35.25, 24.67) * mm, v(-31.87, 22.88) * mm], "startDerivative": vector(3.37, -1.8) * mm, "endDerivative": vector(3.48, -2.85) * mm});
            skFitSpline(sketch, "E129", {"points": [v(-38.11, 23.82) * mm, v(-38.32, 20.66) * mm], "startDerivative": vector(2.21, -2.53) * mm, "endDerivative": vector(-2.53, -2.53) * mm});
            skFitSpline(sketch, "E130", {"points": [v(-38.11, 23.82) * mm, v(-41.7, 22.45) * mm], "startDerivative": vector(-3.48, -0.63) * mm, "endDerivative": vector(-3.59, -1.37) * mm});
            skFitSpline(sketch, "E131", {"points": [v(-41.7, 22.45) * mm, v(-38.32, 20.66) * mm], "startDerivative": vector(3.37, -1.8) * mm, "endDerivative": vector(3.48, -2.85) * mm});
            skFitSpline(sketch, "E132", {"points": [v(-34.37, 30.96) * mm, v(-34.58, 27.8) * mm], "startDerivative": vector(2.21, -2.53) * mm, "endDerivative": vector(-2.53, -2.53) * mm});
            skFitSpline(sketch, "E133", {"points": [v(-34.37, 30.96) * mm, v(-37.95, 29.59) * mm], "startDerivative": vector(-3.48, -0.63) * mm, "endDerivative": vector(-3.59, -1.37) * mm});
            skFitSpline(sketch, "E134", {"points": [v(-37.95, 29.59) * mm, v(-34.58, 27.8) * mm], "startDerivative": vector(3.37, -1.8) * mm, "endDerivative": vector(3.48, -2.85) * mm});
            skFitSpline(sketch, "E135", {"points": [v(-40.15, 34.4) * mm, v(-40.36, 31.24) * mm], "startDerivative": vector(2.21, -2.53) * mm, "endDerivative": vector(-2.53, -2.53) * mm});
            skFitSpline(sketch, "E136", {"points": [v(-40.15, 34.4) * mm, v(-43.74, 33.03) * mm], "startDerivative": vector(-3.48, -0.63) * mm, "endDerivative": vector(-3.59, -1.37) * mm});
            skFitSpline(sketch, "E137", {"points": [v(-43.74, 33.03) * mm, v(-40.36, 31.24) * mm], "startDerivative": vector(3.37, -1.8) * mm, "endDerivative": vector(3.48, -2.85) * mm});
            skFitSpline(sketch, "E138", {"points": [v(-40.74, 28.66) * mm, v(-40.95, 25.5) * mm], "startDerivative": vector(2.21, -2.53) * mm, "endDerivative": vector(-2.53, -2.53) * mm});
            skFitSpline(sketch, "E139", {"points": [v(-40.74, 28.66) * mm, v(-44.33, 27.29) * mm], "startDerivative": vector(-3.48, -0.63) * mm, "endDerivative": vector(-3.59, -1.37) * mm});
            skFitSpline(sketch, "E140", {"points": [v(-44.33, 27.29) * mm, v(-40.95, 25.5) * mm], "startDerivative": vector(3.37, -1.8) * mm, "endDerivative": vector(3.48, -2.85) * mm});
            skFitSpline(sketch, "E141", {"points": [v(-2.56, 33.04) * mm, v(-2.77, 29.88) * mm], "startDerivative": vector(2.21, -2.53) * mm, "endDerivative": vector(-2.53, -2.53) * mm});
            skFitSpline(sketch, "E142", {"points": [v(-2.56, 33.04) * mm, v(-6.14, 31.67) * mm], "startDerivative": vector(-3.48, -0.63) * mm, "endDerivative": vector(-3.59, -1.37) * mm});
            skFitSpline(sketch, "E143", {"points": [v(-6.14, 31.67) * mm, v(-2.77, 29.88) * mm], "startDerivative": vector(3.37, -1.8) * mm, "endDerivative": vector(3.48, -2.85) * mm});
            skFitSpline(sketch, "E144", {"points": [v(-9.58, 31.19) * mm, v(-9.79, 28.02) * mm], "startDerivative": vector(2.21, -2.53) * mm, "endDerivative": vector(-2.53, -2.53) * mm});
            skFitSpline(sketch, "E145", {"points": [v(-9.58, 31.19) * mm, v(-13.16, 29.81) * mm], "startDerivative": vector(-3.48, -0.63) * mm, "endDerivative": vector(-3.59, -1.37) * mm});
            skFitSpline(sketch, "E146", {"points": [v(-13.16, 29.81) * mm, v(-9.79, 28.02) * mm], "startDerivative": vector(3.37, -1.8) * mm, "endDerivative": vector(3.48, -2.85) * mm});
            skFitSpline(sketch, "E147", {"points": [v(-3.6, 27.2) * mm, v(-3.8, 24.03) * mm], "startDerivative": vector(2.21, -2.53) * mm, "endDerivative": vector(-2.53, -2.53) * mm});
            skFitSpline(sketch, "E148", {"points": [v(-3.6, 27.2) * mm, v(-7.18, 25.82) * mm], "startDerivative": vector(-3.48, -0.63) * mm, "endDerivative": vector(-3.59, -1.37) * mm});
            skFitSpline(sketch, "E149", {"points": [v(-7.18, 25.82) * mm, v(-3.8, 24.03) * mm], "startDerivative": vector(3.37, -1.8) * mm, "endDerivative": vector(3.48, -2.85) * mm});
            skFitSpline(sketch, "E150", {"points": [v(2.8, 22.5) * mm, v(2.6, 19.34) * mm], "startDerivative": vector(2.21, -2.53) * mm, "endDerivative": vector(-2.53, -2.53) * mm});
            skFitSpline(sketch, "E151", {"points": [v(2.8, 22.5) * mm, v(-0.78, 21.13) * mm], "startDerivative": vector(-3.48, -0.63) * mm, "endDerivative": vector(-3.59, -1.37) * mm});
            skFitSpline(sketch, "E152", {"points": [v(-0.78, 21.13) * mm, v(2.6, 19.34) * mm], "startDerivative": vector(3.37, -1.8) * mm, "endDerivative": vector(3.48, -2.85) * mm});
            skFitSpline(sketch, "E153", {"points": [v(-4.6, 21.26) * mm, v(-4.82, 18.1) * mm], "startDerivative": vector(2.21, -2.53) * mm, "endDerivative": vector(-2.53, -2.53) * mm});
            skFitSpline(sketch, "E154", {"points": [v(-4.6, 21.26) * mm, v(-8.2, 19.89) * mm], "startDerivative": vector(-3.48, -0.63) * mm, "endDerivative": vector(-3.59, -1.37) * mm});
            skFitSpline(sketch, "E155", {"points": [v(-8.2, 19.89) * mm, v(-4.82, 18.1) * mm], "startDerivative": vector(3.37, -1.8) * mm, "endDerivative": vector(3.48, -2.85) * mm});
            skFitSpline(sketch, "E156", {"points": [v(-12.03, 18.9) * mm, v(-12.24, 15.73) * mm], "startDerivative": vector(2.21, -2.53) * mm, "endDerivative": vector(-2.53, -2.53) * mm});
            skFitSpline(sketch, "E157", {"points": [v(-12.03, 18.9) * mm, v(-15.61, 17.53) * mm], "startDerivative": vector(-3.48, -0.63) * mm, "endDerivative": vector(-3.59, -1.37) * mm});
            skFitSpline(sketch, "E158", {"points": [v(-15.61, 17.53) * mm, v(-12.24, 15.73) * mm], "startDerivative": vector(3.37, -1.8) * mm, "endDerivative": vector(3.48, -2.85) * mm});
            skFitSpline(sketch, "E159", {"points": [v(-10.96, 25.06) * mm, v(-11.17, 21.9) * mm], "startDerivative": vector(2.21, -2.53) * mm, "endDerivative": vector(-2.53, -2.53) * mm});
            skFitSpline(sketch, "E160", {"points": [v(-10.96, 25.06) * mm, v(-14.54, 23.69) * mm], "startDerivative": vector(-3.48, -0.63) * mm, "endDerivative": vector(-3.59, -1.37) * mm});
            skFitSpline(sketch, "E161", {"points": [v(-14.54, 23.69) * mm, v(-11.17, 21.9) * mm], "startDerivative": vector(3.37, -1.8) * mm, "endDerivative": vector(3.48, -2.85) * mm});
            skFitSpline(sketch, "E162", {"points": [v(-16.7, 29.37) * mm, v(-16.92, 26.2) * mm], "startDerivative": vector(2.21, -2.53) * mm, "endDerivative": vector(-2.53, -2.53) * mm});
            skFitSpline(sketch, "E163", {"points": [v(-16.7, 29.37) * mm, v(-20.3, 28) * mm], "startDerivative": vector(-3.48, -0.63) * mm, "endDerivative": vector(-3.59, -1.37) * mm});
            skFitSpline(sketch, "E164", {"points": [v(-20.3, 28) * mm, v(-16.92, 26.2) * mm], "startDerivative": vector(3.37, -1.8) * mm, "endDerivative": vector(3.48, -2.85) * mm});
            skFitSpline(sketch, "E165", {"points": [v(-18.1, 23.56) * mm, v(-18.3, 20.4) * mm], "startDerivative": vector(2.21, -2.53) * mm, "endDerivative": vector(-2.53, -2.53) * mm});
            skFitSpline(sketch, "E166", {"points": [v(-18.1, 23.56) * mm, v(-21.68, 22.2) * mm], "startDerivative": vector(-3.48, -0.63) * mm, "endDerivative": vector(-3.59, -1.37) * mm});
            skFitSpline(sketch, "E167", {"points": [v(-21.68, 22.2) * mm, v(-18.3, 20.4) * mm], "startDerivative": vector(3.37, -1.8) * mm, "endDerivative": vector(3.48, -2.85) * mm});
            skFitSpline(sketch, "E168", {"points": [v(-25.55, 22.9) * mm, v(-25.76, 19.74) * mm], "startDerivative": vector(2.21, -2.53) * mm, "endDerivative": vector(-2.53, -2.53) * mm});
            skFitSpline(sketch, "E169", {"points": [v(-25.55, 22.9) * mm, v(-29.13, 21.54) * mm], "startDerivative": vector(-3.48, -0.63) * mm, "endDerivative": vector(-3.59, -1.37) * mm});
            skFitSpline(sketch, "E170", {"points": [v(-29.13, 21.54) * mm, v(-25.76, 19.74) * mm], "startDerivative": vector(3.37, -1.8) * mm, "endDerivative": vector(3.48, -2.85) * mm});
            skFitSpline(sketch, "E171", {"points": [v(-33.2, 19.84) * mm, v(-33.4, 16.67) * mm], "startDerivative": vector(2.21, -2.53) * mm, "endDerivative": vector(-2.53, -2.53) * mm});
            skFitSpline(sketch, "E172", {"points": [v(-33.2, 19.84) * mm, v(-36.78, 18.47) * mm], "startDerivative": vector(-3.48, -0.63) * mm, "endDerivative": vector(-3.59, -1.37) * mm});
            skFitSpline(sketch, "E173", {"points": [v(-36.78, 18.47) * mm, v(-33.4, 16.67) * mm], "startDerivative": vector(3.37, -1.8) * mm, "endDerivative": vector(3.48, -2.85) * mm});
            skFitSpline(sketch, "E174", {"points": [v(-27.18, 17.2) * mm, v(-27.39, 14.04) * mm], "startDerivative": vector(2.21, -2.53) * mm, "endDerivative": vector(-2.53, -2.53) * mm});
            skFitSpline(sketch, "E175", {"points": [v(-27.18, 17.2) * mm, v(-30.76, 15.83) * mm], "startDerivative": vector(-3.48, -0.63) * mm, "endDerivative": vector(-3.59, -1.37) * mm});
            skFitSpline(sketch, "E176", {"points": [v(-30.76, 15.83) * mm, v(-27.39, 14.04) * mm], "startDerivative": vector(3.37, -1.8) * mm, "endDerivative": vector(3.48, -2.85) * mm});
            skFitSpline(sketch, "E177", {"points": [v(-19.52, 17.82) * mm, v(-19.73, 14.65) * mm], "startDerivative": vector(2.21, -2.53) * mm, "endDerivative": vector(-2.53, -2.53) * mm});
            skFitSpline(sketch, "E178", {"points": [v(-19.52, 17.82) * mm, v(-23.1, 16.45) * mm], "startDerivative": vector(-3.48, -0.63) * mm, "endDerivative": vector(-3.59, -1.37) * mm});
            skFitSpline(sketch, "E179", {"points": [v(-23.1, 16.45) * mm, v(-19.73, 14.65) * mm], "startDerivative": vector(3.37, -1.8) * mm, "endDerivative": vector(3.48, -2.85) * mm});
            skFitSpline(sketch, "E180", {"points": [v(3.8, 28.2) * mm, v(3.6, 25.05) * mm], "startDerivative": vector(2.21, -2.53) * mm, "endDerivative": vector(-2.53, -2.53) * mm});
            skFitSpline(sketch, "E181", {"points": [v(3.8, 28.2) * mm, v(0.22, 26.84) * mm], "startDerivative": vector(-3.48, -0.63) * mm, "endDerivative": vector(-3.59, -1.37) * mm});
            skFitSpline(sketch, "E182", {"points": [v(0.22, 26.84) * mm, v(3.6, 25.05) * mm], "startDerivative": vector(3.37, -1.8) * mm, "endDerivative": vector(3.48, -2.85) * mm});
            skFitSpline(sketch, "E183", {"points": [v(9.8, 22.32) * mm, v(9.6, 19.16) * mm], "startDerivative": vector(2.21, -2.53) * mm, "endDerivative": vector(-2.53, -2.53) * mm});
            skFitSpline(sketch, "E184", {"points": [v(9.8, 22.32) * mm, v(6.22, 20.95) * mm], "startDerivative": vector(-3.48, -0.63) * mm, "endDerivative": vector(-3.59, -1.37) * mm});
            skFitSpline(sketch, "E185", {"points": [v(6.22, 20.95) * mm, v(9.6, 19.16) * mm], "startDerivative": vector(3.37, -1.8) * mm, "endDerivative": vector(3.48, -2.85) * mm});
            skFitSpline(sketch, "E186", {"points": [v(5, 34.17) * mm, v(4.79, 31) * mm], "startDerivative": vector(2.21, -2.53) * mm, "endDerivative": vector(-2.53, -2.53) * mm});
            skFitSpline(sketch, "E187", {"points": [v(5, 34.17) * mm, v(1.41, 32.8) * mm], "startDerivative": vector(-3.48, -0.63) * mm, "endDerivative": vector(-3.59, -1.37) * mm});
            skFitSpline(sketch, "E188", {"points": [v(1.41, 32.8) * mm, v(4.79, 31) * mm], "startDerivative": vector(3.37, -1.8) * mm, "endDerivative": vector(3.48, -2.85) * mm});
            skFitSpline(sketch, "E189", {"points": [v(12.12, 34.5) * mm, v(11.91, 31.34) * mm], "startDerivative": vector(2.21, -2.53) * mm, "endDerivative": vector(-2.53, -2.53) * mm});
            skFitSpline(sketch, "E190", {"points": [v(12.12, 34.5) * mm, v(8.54, 33.13) * mm], "startDerivative": vector(-3.48, -0.63) * mm, "endDerivative": vector(-3.59, -1.37) * mm});
            skFitSpline(sketch, "E191", {"points": [v(8.54, 33.13) * mm, v(11.91, 31.34) * mm], "startDerivative": vector(3.37, -1.8) * mm, "endDerivative": vector(3.48, -2.85) * mm});
            skFitSpline(sketch, "E192", {"points": [v(10.78, 28.47) * mm, v(10.56, 25.3) * mm], "startDerivative": vector(2.21, -2.53) * mm, "endDerivative": vector(-2.53, -2.53) * mm});
            skFitSpline(sketch, "E193", {"points": [v(10.78, 28.47) * mm, v(7.2, 27.1) * mm], "startDerivative": vector(-3.48, -0.63) * mm, "endDerivative": vector(-3.59, -1.37) * mm});
            skFitSpline(sketch, "E194", {"points": [v(7.2, 27.1) * mm, v(10.56, 25.3) * mm], "startDerivative": vector(3.37, -1.8) * mm, "endDerivative": vector(3.48, -2.85) * mm});
            skFitSpline(sketch, "E195", {"points": [v(19.2, 33.97) * mm, v(19, 30.8) * mm], "startDerivative": vector(2.21, -2.53) * mm, "endDerivative": vector(-2.53, -2.53) * mm});
            skFitSpline(sketch, "E196", {"points": [v(19.2, 33.97) * mm, v(15.62, 32.6) * mm], "startDerivative": vector(-3.48, -0.63) * mm, "endDerivative": vector(-3.59, -1.37) * mm});
            skFitSpline(sketch, "E197", {"points": [v(15.62, 32.6) * mm, v(19, 30.8) * mm], "startDerivative": vector(3.37, -1.8) * mm, "endDerivative": vector(3.48, -2.85) * mm});
            skFitSpline(sketch, "E198", {"points": [v(26.05, 32.91) * mm, v(25.84, 29.75) * mm], "startDerivative": vector(2.21, -2.53) * mm, "endDerivative": vector(-2.53, -2.53) * mm});
            skFitSpline(sketch, "E199", {"points": [v(26.05, 32.91) * mm, v(22.46, 31.54) * mm], "startDerivative": vector(-3.48, -0.63) * mm, "endDerivative": vector(-3.59, -1.37) * mm});
            skFitSpline(sketch, "E200", {"points": [v(22.46, 31.54) * mm, v(25.84, 29.75) * mm], "startDerivative": vector(3.37, -1.8) * mm, "endDerivative": vector(3.48, -2.85) * mm});
            skFitSpline(sketch, "E201", {"points": [v(31.33, 25.92) * mm, v(31.11, 22.75) * mm], "startDerivative": vector(2.21, -2.53) * mm, "endDerivative": vector(-2.53, -2.53) * mm});
            skFitSpline(sketch, "E202", {"points": [v(31.33, 25.92) * mm, v(27.74, 24.55) * mm], "startDerivative": vector(-3.48, -0.63) * mm, "endDerivative": vector(-3.59, -1.37) * mm});
            skFitSpline(sketch, "E203", {"points": [v(27.74, 24.55) * mm, v(31.11, 22.75) * mm], "startDerivative": vector(3.37, -1.8) * mm, "endDerivative": vector(3.48, -2.85) * mm});
            skFitSpline(sketch, "E204", {"points": [v(23.5, 21.62) * mm, v(23.3, 18.45) * mm], "startDerivative": vector(2.21, -2.53) * mm, "endDerivative": vector(-2.53, -2.53) * mm});
            skFitSpline(sketch, "E205", {"points": [v(23.5, 21.62) * mm, v(19.92, 20.25) * mm], "startDerivative": vector(-3.48, -0.63) * mm, "endDerivative": vector(-3.59, -1.37) * mm});
            skFitSpline(sketch, "E206", {"points": [v(19.92, 20.25) * mm, v(23.3, 18.45) * mm], "startDerivative": vector(3.37, -1.8) * mm, "endDerivative": vector(3.48, -2.85) * mm});
            skFitSpline(sketch, "E207", {"points": [v(24.76, 27.03) * mm, v(24.54, 23.86) * mm], "startDerivative": vector(2.21, -2.53) * mm, "endDerivative": vector(-2.53, -2.53) * mm});
            skFitSpline(sketch, "E208", {"points": [v(24.76, 27.03) * mm, v(21.17, 25.65) * mm], "startDerivative": vector(-3.48, -0.63) * mm, "endDerivative": vector(-3.59, -1.37) * mm});
            skFitSpline(sketch, "E209", {"points": [v(21.17, 25.65) * mm, v(24.54, 23.86) * mm], "startDerivative": vector(3.37, -1.8) * mm, "endDerivative": vector(3.48, -2.85) * mm});
            skFitSpline(sketch, "E210", {"points": [v(17.98, 28.16) * mm, v(17.77, 25) * mm], "startDerivative": vector(2.21, -2.53) * mm, "endDerivative": vector(-2.53, -2.53) * mm});
            skFitSpline(sketch, "E211", {"points": [v(17.98, 28.16) * mm, v(14.4, 26.79) * mm], "startDerivative": vector(-3.48, -0.63) * mm, "endDerivative": vector(-3.59, -1.37) * mm});
            skFitSpline(sketch, "E212", {"points": [v(14.4, 26.79) * mm, v(17.77, 25) * mm], "startDerivative": vector(3.37, -1.8) * mm, "endDerivative": vector(3.48, -2.85) * mm});
            skFitSpline(sketch, "E213", {"points": [v(16.81, 22.5) * mm, v(16.6, 19.34) * mm], "startDerivative": vector(2.21, -2.53) * mm, "endDerivative": vector(-2.53, -2.53) * mm});
            skFitSpline(sketch, "E214", {"points": [v(16.81, 22.5) * mm, v(13.23, 21.13) * mm], "startDerivative": vector(-3.48, -0.63) * mm, "endDerivative": vector(-3.59, -1.37) * mm});
            skFitSpline(sketch, "E215", {"points": [v(13.23, 21.13) * mm, v(16.6, 19.34) * mm], "startDerivative": vector(3.37, -1.8) * mm, "endDerivative": vector(3.48, -2.85) * mm});
            skFitSpline(sketch, "E216", {"points": [v(57.65, 29.4) * mm, v(57.99, 31.77) * mm, v(60.23, 32.25) * mm, v(62.85, 30.12) * mm], "startDerivative": vector(-5.28, 7.03) * mm, "endDerivative": vector(6.45, -6.69) * mm});
            skLineSegment(sketch, "E217", {"start": v(57.65, 29.4) * mm, "end": v(62.85, 30.12) * mm});
            skFitSpline(sketch, "E218", {"points": [v(66.89, 31.16) * mm, v(66.7, 31.9) * mm, v(68.15, 33.34) * mm, v(69.84, 32.17) * mm], "startDerivative": vector(-1.34, 1.86) * mm, "endDerivative": vector(3.1, -4.88) * mm});
            skLineSegment(sketch, "E219", {"start": v(66.89, 31.16) * mm, "end": v(69.84, 32.17) * mm});
            skSolve(sketch);
        }
        {
            var Q0;
            Q0 = qSketchRegion(id + "F6", true);
            extrude(context, id + "F7", {"entities" : qUnion([Q0]), "operationType" : NewBodyOperationType.REMOVE, "oppositeDirection" : true, "depth" : 25.35 * mm});
        }
        {
            var Q0;
            Q0=makeQuery(id+"F3.opExtrude","CAP_FACE",FACE,{"disambiguationData":[OSD([sQuery(id+"F2.wireOp",EDGE,"E58"),sQuery(id+"F2.wireOp",EDGE,"E59"),sQuery(id+"F2.wireOp",EDGE,"E60"),sQuery(id+"F2.wireOp",EDGE,"E61"),sQuery(id+"F2.wireOp",EDGE,"E62"),sQuery(id+"F2.wireOp",EDGE,"E63"),sQuery(id+"F2.wireOp",EDGE,"E64"),sQuery(id+"F2.wireOp",EDGE,"E65"),sQuery(id+"F2.wireOp",EDGE,"E66"),sQuery(id+"F2.wireOp",EDGE,"E67"),sQuery(id+"F2.wireOp",EDGE,"E68"),sQuery(id+"F2.wireOp",EDGE,"E69"),sQuery(id+"F2.wireOp",EDGE,"E70"),sQuery(id+"F2.wireOp",EDGE,"E71"),sQuery(id+"F2.wireOp",EDGE,"E72"),sQuery(id+"F2.wireOp",EDGE,"E73"),sQuery(id+"F2.wireOp",EDGE,"E74"),sQuery(id+"F2.wireOp",EDGE,"E75.trimOffspring"),sQuery(id+"F2.wireOp",EDGE,"E76"),sQuery(id+"F2.wireOp",EDGE,"E77"),sQuery(id+"F2.wireOp",EDGE,"E75.trimOffspring"),sQuery(id+"F2.wireOp",EDGE,"E78"),sQuery(id+"F2.wireOp",EDGE,"E79"),sQuery(id+"F2.wireOp",EDGE,"E80"),sQuery(id+"F2.wireOp",EDGE,"E81"),sQuery(id+"F2.wireOp",EDGE,"E82"),sQuery(id+"F2.wireOp",EDGE,"E83"),sQuery(id+"F2.wireOp",EDGE,"E84"),sQuery(id+"F2.wireOp",EDGE,"E85"),sQuery(id+"F2.wireOp",EDGE,"E86"),sQuery(id+"F2.wireOp",EDGE,"E87"),sQuery(id+"F2.wireOp",EDGE,"E88"),sQuery(id+"F2.wireOp",EDGE,"E89"),sQuery(id+"F2.wireOp",EDGE,"E90"),sQuery(id+"F2.wireOp",EDGE,"E91"),sQuery(id+"F2.wireOp",EDGE,"E92"),sQuery(id+"F2.wireOp",EDGE,"E93"),sQuery(id+"F2.wireOp",EDGE,"E94")])],"isStart":false});
            var sketch = newSketch(context, id + "F8", { "sketchPlane" : qUnion([Q0])});
            skFitSpline(sketch, "E220", {"points": [v(40.94, 20.77) * mm, v(42.93, 18.87) * mm, v(45.56, 18.5) * mm, v(47.74, 19.68) * mm, v(52.09, 22.13) * mm, v(58.8, 22.4) * mm, v(65.5, 20.44) * mm], "startDerivative": vector(13.14, -16.45) * mm, "endDerivative": vector(31.93, -3.54) * mm});
            skFitSpline(sketch, "E221", {"points": [v(40.94, 20.77) * mm, v(40.32, 19.96) * mm, v(40.94, 18.27) * mm, v(43.78, 16.82) * mm, v(47.05, 17.33) * mm, v(50.35, 19.28) * mm, v(52.04, 19.73) * mm, v(54.93, 18.6) * mm, v(59.32, 14.5) * mm, v(64.86, 10.54) * mm, v(67.58, 10.09) * mm, v(69.54, 11.08) * mm, v(70.7, 10.6) * mm, v(71.68, 9.03) * mm, v(72.42, 8.7) * mm, v(73.58, 9.86) * mm, v(74.6, 10.09) * mm, v(75.79, 8.23) * mm, v(76.46, 7.68) * mm, v(78.32, 8.87) * mm, v(79.44, 8.84) * mm, v(80.37, 6.98) * mm, v(81.17, 6.7) * mm, v(82.9, 7.9) * mm, v(83.73, 7.81) * mm, v(84.92, 5.8) * mm, v(85.88, 5.8) * mm, v(87.03, 6.85) * mm, v(87.93, 6.91) * mm, v(89.41, 5.82) * mm, v(91.27, 5.79) * mm, v(91.34, 6.5) * mm, v(90.34, 7.26) * mm], "startDerivative": vector(-35.56, -30.24) * mm, "endDerivative": vector(-47.98, 26.55) * mm});
            skFitSpline(sketch, "E222", {"points": [v(90.34, 7.26) * mm, v(69.83, 13.3) * mm], "startDerivative": vector(-20.5, 6.04) * mm, "endDerivative": vector(-20.5, 6.04) * mm});
            skFitSpline(sketch, "E223", {"points": [v(69.83, 13.3) * mm, v(68.11, 14.56) * mm, v(66.2, 17.35) * mm, v(66.17, 18.27) * mm], "startDerivative": vector(-4.82, 2.8) * mm, "endDerivative": vector(0.64, 3.5) * mm});
            skFitSpline(sketch, "E224", {"points": [v(58.8, 22.4) * mm, v(63.21, 21.03) * mm, v(64.2, 20.38) * mm, v(65.17, 20.2) * mm], "startDerivative": vector(10.4, -2.6) * mm, "endDerivative": vector(4.41, -0.33) * mm});
            skLineSegment(sketch, "E225", {"start": v(66.17, 18.27) * mm, "end": v(65.17, 20.2) * mm});
            skSolve(sketch);
        }
        {
            var Q0;
            Q0 = qSketchRegion(id + "F8", true);
            extrude(context, id + "F9", {"entities" : qUnion([Q0]), "operationType" : NewBodyOperationType.REMOVE, "oppositeDirection" : true, "depth" : 25.35 * mm});
        }
        {
            var Q0;
            Q0=qCreatedBy(makeId("Top.planeOp"),FACE);
            var sketch = newSketch(context, id + "F10", { "sketchPlane" : qUnion([Q0])});
            skFitSpline(sketch, "E226", {"points": [v(64.77, 20.79) * mm, v(66.63, 17.2) * mm, v(68.68, 15.18) * mm, v(76.53, 13.89) * mm, v(85.84, 9.5) * mm, v(93.94, 7.8) * mm, v(92.02, 4.17) * mm, v(84.19, 3.14) * mm, v(62.97, 6.23) * mm, v(51.7, 14.91) * mm, v(44, 15.34) * mm, v(37.82, 18.48) * mm, v(40.46, 22.72) * mm, v(44, 20.8) * mm, v(53.23, 25.58) * mm, v(64.77, 20.79) * mm]});
            skSolve(sketch);
        }
        {
            var Q0;
            Q0 = qSketchRegion(id + "F10", true);
            extrude(context, id + "F11", {"entities" : qUnion([Q0]), "depth" : 1.27 * mm});
        }
    });
